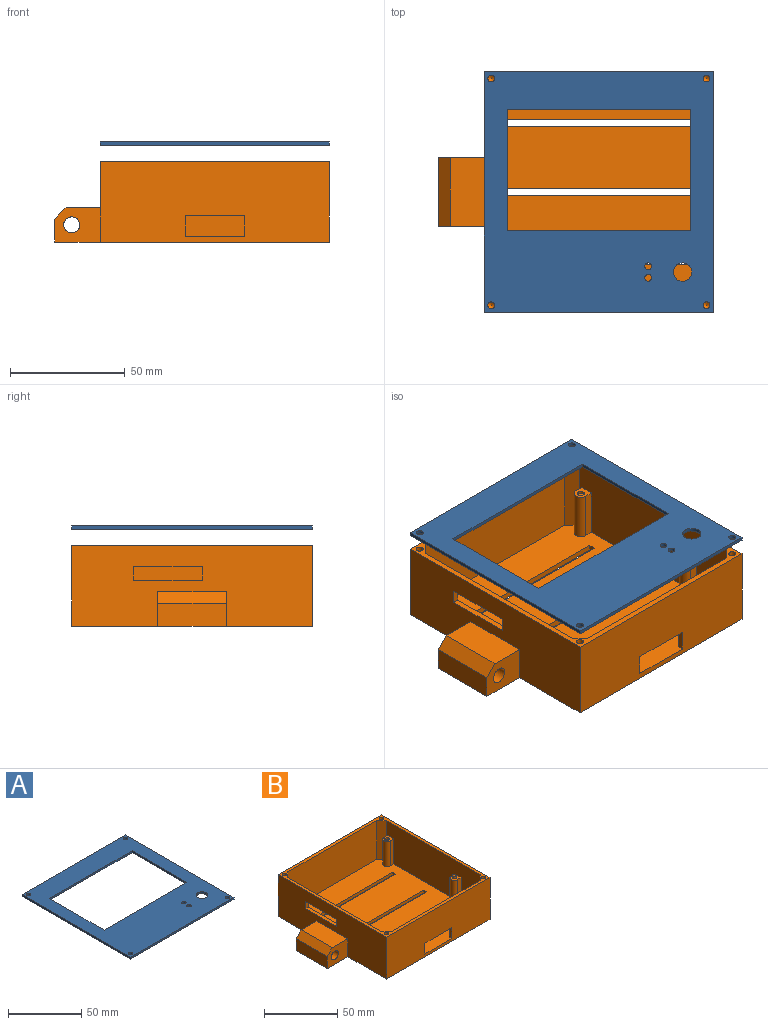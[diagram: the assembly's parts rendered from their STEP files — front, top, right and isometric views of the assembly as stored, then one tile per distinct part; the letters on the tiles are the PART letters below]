
ASSEMBLY  parts=2 mates=2
PART A: 17 faces, bbox 100x105x1.5 mm
  f0: plane 105x100mm, normal (0,0,1), area 6167.3mm2, adj f2,f3,f4,f5,f6,f7,f8,f9
  f1: plane 105x100mm, normal (0,0,-1), area 6167.3mm2, adj f2,f3,f4,f5,f6,f7,f8,f9
  f2: plane 105x1.5mm, normal (1,0,0), area 157.5mm2, adj f0,f1,f3,f5
  f3: plane 100x1.5mm, normal (0,1,0), area 150mm2, adj f0,f1,f2,f4
  f4: plane 105x1.5mm, normal (-1,0,0), area 157.5mm2, adj f0,f1,f3,f5
  f5: plane 100x1.5mm, normal (0,-1,0), area 150mm2, adj f0,f1,f2,f4
  f6: cylinder r=1.5mm len=3mm, axis (0,0,1), area 14.1mm2, adj f0,f1
  f7: cylinder r=1.5mm len=3mm, axis (0,0,1), area 14.1mm2, adj f0,f1
  f8: cylinder r=1.5mm len=3mm, axis (0,0,1), area 14.1mm2, adj f0,f1
  f9: cylinder r=1.5mm len=3mm, axis (0,0,1), area 14.1mm2, adj f0,f1
  f10: plane 53x1.5mm, normal (-1,0,0), area 79.5mm2, adj f0,f1,f11,f13
  f11: plane 80x1.5mm, normal (0,-1,0), area 120mm2, adj f0,f1,f10,f12
  f12: plane 53x1.5mm, normal (1,0,0), area 79.5mm2, adj f0,f1,f11,f13
  f13: plane 80x1.5mm, normal (0,1,0), area 120mm2, adj f0,f1,f10,f12
  f14: cylinder r=4mm len=8mm, axis (0,0,1), area 37.7mm2, adj f0,f1
  f15: cylinder r=1.5mm len=3mm, axis (0,0,1), area 14.1mm2, adj f0,f1
  f16: cylinder r=1.5mm len=3mm, axis (0,0,1), area 14.1mm2, adj f0,f1
PART B: 74 faces, bbox 120x105x35 mm
  f0: plane 102.5x95mm, normal (0,0,1), area 8664mm2, adj f2,f3,f4,f9,f10,f11,f12,f13
  f1: plane 120x105mm, normal (0,0,-1), area 10380mm2, adj f2,f6,f7,f8,f56,f58,f59,f62
  f2: plane 100x35mm, normal (0,-1,0), area 3266mm2, adj f0,f1,f5,f6,f8,f41,f42,f43
  f3: plane 86x32.5mm, normal (0,1,0), area 2561mm2, adj f0,f5,f11,f14,f41,f42,f43
  f4: plane 91x32.5mm, normal (1,0,0), area 2525.5mm2, adj f0,f5,f13,f14,f15,f16,f18,f19
  f5: plane 105x100mm, normal (0,0,1), area 1012.2mm2, adj f2,f3,f4,f6,f7,f8,f9,f10
  f6: plane 105x35mm, normal (1,0,0), area 3675mm2, adj f1,f2,f5,f7
  f7: plane 100x35mm, normal (0,1,0), area 3500mm2, adj f1,f5,f6,f8
  f8: plane 105x35mm, normal (-1,0,0), area 3045mm2, adj f1,f2,f5,f7,f52,f53,f54,f55
  f9: plane 91x32.5mm, normal (-1,0,0), area 2705.5mm2, adj f0,f5,f11,f12,f23,f25,f26,f27
  f10: plane 86x32.5mm, normal (0,-1,0), area 2795mm2, adj f0,f5,f12,f13
  f11: plane 32.5x4.5mm, normal (-0.71,0.71,0), area 206.8mm2, adj f0,f3,f5,f9
  f12: plane 32.5x4.5mm, normal (-0.71,-0.71,0), area 206.8mm2, adj f0,f5,f9,f10
  f13: plane 32.5x4.5mm, normal (0.71,-0.71,0), area 206.8mm2, adj f0,f4,f5,f10
  f14: plane 32.5x4.5mm, normal (0.71,0.71,0), area 206.8mm2, adj f0,f3,f4,f5
  f15: plane 21x3.5mm, normal (0,1,0), area 73.5mm2, adj f0,f4,f17,f18
  f16: plane 21x3.5mm, normal (0,-1,0), area 73.5mm2, adj f0,f4,f17,f18
  f17: cylinder r=3mm len=21mm, axis (0,0,-1), area 197.9mm2, adj f0,f15,f16,f18
  f18: plane 6.5x6mm, normal (0,0,1), area 28.1mm2, adj f4,f15,f16,f17,f33
  f19: plane 21x3.5mm, normal (0,-1,0), area 73.5mm2, adj f0,f4,f20,f22
  f20: cylinder r=3mm len=21mm, axis (0,0,-1), area 197.9mm2, adj f0,f19,f21,f22
  f21: plane 21x3.5mm, normal (0,1,0), area 73.5mm2, adj f0,f4,f20,f22
  f22: plane 6.5x6mm, normal (0,0,1), area 30.2mm2, adj f4,f19,f20,f21,f35
  f23: plane 21x3.5mm, normal (0,1,0), area 73.5mm2, adj f0,f9,f24,f26
  f24: cylinder r=3mm len=21mm, axis (0,0,-1), area 197.9mm2, adj f0,f23,f25,f26
  f25: plane 21x3.5mm, normal (0,-1,0), area 73.5mm2, adj f0,f9,f24,f26
  f26: plane 6.5x6mm, normal (0,0,1), area 30.2mm2, adj f9,f23,f24,f25,f37
  f27: plane 21x3.5mm, normal (0,-1,0), area 73.5mm2, adj f0,f9,f29,f30
  f28: plane 21x3.5mm, normal (0,1,0), area 73.5mm2, adj f0,f9,f29,f30
  f29: cylinder r=3mm len=21mm, axis (0,0,-1), area 197.9mm2, adj f0,f27,f28,f30
  f30: plane 6.5x6mm, normal (0,0,1), area 28.1mm2, adj f9,f27,f28,f29,f31
  f31: cylinder r=1.5mm len=3mm, axis (0,0,1), area 9.4mm2, adj f30,f32
  f32: plane 3x3mm, normal (0,0,1), area 7.1mm2, adj f31
  f33: cylinder r=1.5mm len=3mm, axis (0,0,1), area 9.4mm2, adj f18,f34
  f34: plane 3x3mm, normal (0,0,1), area 7.1mm2, adj f33
  f35: cylinder r=1.25mm len=2.5mm, axis (0,0,-1), area 15.7mm2, adj f22,f40
  f36: plane 0.5x0.5mm, normal (0,0,1), area 0.2mm2, adj f40
  f37: cylinder r=1.25mm len=2.5mm, axis (0,0,-1), area 15.7mm2, adj f26,f39
  f38: plane 0.5x0.5mm, normal (0,0,1), area 0.2mm2, adj f39
  f39: cone r=0.25mm half-angle=45deg, axis (0,0,-1), area 6.7mm2, adj f37,f38
  f40: cone r=0.25mm half-angle=45deg, axis (0,0,-1), area 6.7mm2, adj f35,f36
  f41: plane 9x2.5mm, normal (-1,0,0), area 22.5mm2, adj f0,f2,f3,f43
  f42: plane 9x2.5mm, normal (1,0,0), area 22.5mm2, adj f0,f2,f3,f43
  f43: plane 26x2.5mm, normal (0,0,-1), area 65mm2, adj f2,f3,f41,f42
  f44: cone r=0mm half-angle=59deg, axis (0,0,1), area 8.2mm2, adj f45
  f45: cylinder r=1.5mm len=15mm, axis (0,0,1), area 141.4mm2, adj f5,f44
  f46: cone r=0mm half-angle=59deg, axis (0,0,1), area 8.2mm2, adj f47
  f47: cylinder r=1.5mm len=15mm, axis (0,0,1), area 141.4mm2, adj f5,f46
  f48: cone r=0mm half-angle=59deg, axis (0,0,1), area 8.2mm2, adj f49
  f49: cylinder r=1.5mm len=15mm, axis (0,0,1), area 141.4mm2, adj f5,f48
  f50: cone r=0mm half-angle=59deg, axis (0,0,1), area 8.2mm2, adj f51
  f51: cylinder r=1.5mm len=15mm, axis (0,0,1), area 141.4mm2, adj f5,f50
  f52: plane 6x2.5mm, normal (0,-1,0), area 15mm2, adj f4,f8,f53,f54
  f53: plane 30x2.5mm, normal (0,0,-1), area 75mm2, adj f4,f8,f52,f55
  f54: plane 30x2.5mm, normal (0,0,1), area 75mm2, adj f4,f8,f52,f55
  f55: plane 6x2.5mm, normal (0,1,0), area 15mm2, adj f4,f8,f53,f54
  f56: plane 20x15mm, normal (0,-1,0), area 249mm2, adj f1,f8,f57,f59,f60,f61
  f57: plane 30x15mm, normal (0,0,1), area 450mm2, adj f8,f56,f58,f61
  f58: plane 20x15mm, normal (0,1,0), area 249mm2, adj f1,f8,f57,f59,f60,f61
  f59: plane 30x10mm, normal (-1,0,0), area 300mm2, adj f1,f56,f58,f61
  f60: cylinder r=3.5mm len=30mm, axis (0,1,0), area 659.7mm2, adj f56,f58
  f61: plane 30x5mm, normal (-0.71,0,0.71), area 212.1mm2, adj f56,f57,f58,f59
  f62: plane 80x2.5mm, normal (0,-1,0), area 200mm2, adj f0,f1,f63,f65
  f63: plane 3x2.5mm, normal (1,0,0), area 7.5mm2, adj f0,f1,f62,f64
  f64: plane 80x2.5mm, normal (0,1,0), area 200mm2, adj f0,f1,f63,f65
  f65: plane 3x2.5mm, normal (-1,0,0), area 7.5mm2, adj f0,f1,f62,f64
  f66: plane 3x2.5mm, normal (-1,0,0), area 7.5mm2, adj f0,f1,f67,f69
  f67: plane 80x2.5mm, normal (0,-1,0), area 200mm2, adj f0,f1,f66,f68
  f68: plane 3x2.5mm, normal (1,0,0), area 7.5mm2, adj f0,f1,f67,f69
  f69: plane 80x2.5mm, normal (0,1,0), area 200mm2, adj f0,f1,f66,f68
  f70: plane 3x2.5mm, normal (-1,0,0), area 7.5mm2, adj f0,f1,f71,f73
  f71: plane 80x2.5mm, normal (0,-1,0), area 200mm2, adj f0,f1,f70,f72
  f72: plane 3x2.5mm, normal (1,0,0), area 7.5mm2, adj f0,f1,f71,f73
  f73: plane 80x2.5mm, normal (0,1,0), area 200mm2, adj f0,f1,f70,f72
PLACE A t=(45.94,32.3,-0.88)mm
PLACE B t=(45.94,32.3,-43.09)mm
MATE cylindrical A.f9 <-> B.f46  axis (0,0,1) through (92.94,81.8,-0.13)mm
MATE cylindrical A.f7 <-> B.f48  axis (0,0,1) through (92.94,-17.2,-0.13)mm
